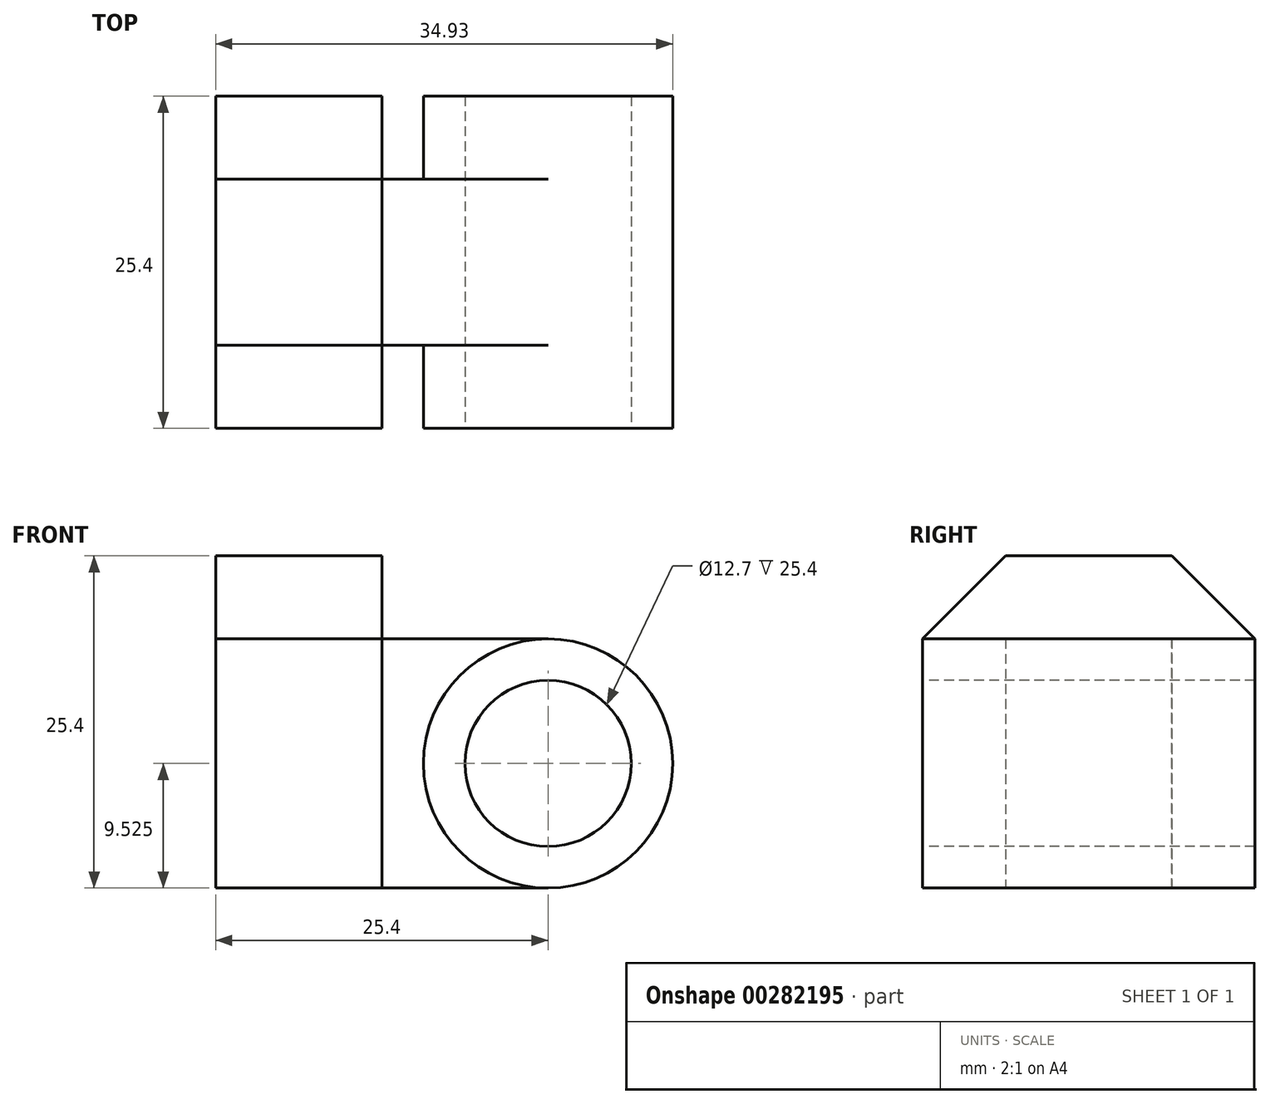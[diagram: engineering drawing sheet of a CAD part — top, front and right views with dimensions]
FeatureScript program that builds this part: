
annotation { "Feature Type Name" : "Feature", "Feature Type Description" : "" }
export const myFeature = defineFeature(function(context is Context, id is Id, definition is map)
    precondition{}
    {
        {
            var Q0;
            Q0=qCreatedBy(makeId("Right.planeOp"),FACE);
            var sketch = newSketch(context, id + "F0", { "sketchPlane" : qUnion([Q0])});
            skLineSegment(sketch, "E0", {"start": v(-12.7, 0) * mm, "end": v(12.7, 0) * mm});
            skLineSegment(sketch, "E1", {"start": v(12.7, 0) * mm, "end": v(12.7, 19.05) * mm});
            skLineSegment(sketch, "E2", {"start": v(-12.7, 19.05) * mm, "end": v(-12.7, 0) * mm});
            skLineSegment(sketch, "E3", {"start": v(12.7, 19.05) * mm, "end": v(6.35, 25.4) * mm});
            skLineSegment(sketch, "E4", {"start": v(6.35, 25.4) * mm, "end": v(-6.35, 25.4) * mm});
            skLineSegment(sketch, "E5", {"start": v(-6.35, 25.4) * mm, "end": v(-12.7, 19.05) * mm});
            skLineSegment(sketch, "E6", {"start": v(0, 0) * mm, "end": v(0, 25.4) * mm, "construction": true});
            skSolve(sketch);
        }
        {
            var Q0;
            Q0=makeQuery(id+"F0.imprint","IMPRINT",FACE,{"disambiguationData":[TD([[makeQuery(id+"F0.imprint","IMPRINT",EDGE,{"derivedFrom":sQuery(id+"F0.wireOp",EDGE,"E0")}),1.0]])]});
            extrude(context, id + "F1", {"entities" : qUnion([Q0]), "depth" : 12.7 * mm});
        }
        {
            var Q0;
            Q0=makeQuery(id+"F1.opExtrude","CAP_FACE",FACE,{"disambiguationData":[OSD([sQuery(id+"F0.wireOp",EDGE,"E0"),sQuery(id+"F0.wireOp",EDGE,"E1"),sQuery(id+"F0.wireOp",EDGE,"E2"),sQuery(id+"F0.wireOp",EDGE,"E3"),sQuery(id+"F0.wireOp",EDGE,"E4"),sQuery(id+"F0.wireOp",EDGE,"E5")])],"isStart":false});
            var sketch = newSketch(context, id + "F2", { "sketchPlane" : qUnion([Q0])});
            skLineSegment(sketch, "E7.bottom", {"start": v(-6.35, 19.05) * mm, "end": v(6.35, 19.05) * mm});
            skLineSegment(sketch, "E7.top", {"start": v(-6.35, 0) * mm, "end": v(6.35, 0) * mm});
            skLineSegment(sketch, "E7.left", {"start": v(-6.35, 19.05) * mm, "end": v(-6.35, 0) * mm});
            skLineSegment(sketch, "E7.right", {"start": v(6.35, 19.05) * mm, "end": v(6.35, 0) * mm});
            skSolve(sketch);
        }
        {
            var Q0;
            Q0=makeQuery(id+"F2.imprint","IMPRINT",FACE,{"disambiguationData":[TD([[makeQuery(id+"F2.imprint","IMPRINT",EDGE,{"derivedFrom":sQuery(id+"F2.wireOp",EDGE,"E7.bottom")}),-1.0]])]});
            extrude(context, id + "F3", {"entities" : qUnion([Q0]), "operationType" : NewBodyOperationType.ADD, "depth" : 12.7 * mm});
        }
        {
            var Q0;
            Q0=makeQuery(id+"F3.opExtrude","SWEPT_FACE",FACE,{"disambiguationData":[OSD([sQuery(id+"F2.wireOp",EDGE,"E7.left")])]});
            var sketch = newSketch(context, id + "F4", { "sketchPlane" : qUnion([Q0])});
            skCircle(sketch, "E8", {"center": v(25.4, 9.53) * mm, "radius": 6.35 * mm});
            skCircle(sketch, "E9", {"center": v(25.4, 9.53) * mm, "radius": 9.53 * mm});
            skSolve(sketch);
        }
        {
            var Q0;
            {var subQ0=sQuery(id+"F4.wireOp",EDGE,"E8");var subQ1=makeQuery(id+"F3.opExtrude","CAP_EDGE",EDGE,{"disambiguationData":[OSD([sQuery(id+"F2.wireOp",EDGE,"E7.left")])],"isStart":false});var subQ2=makeQuery(id+"F4.imprint","INTERSECT",VERTEX,{"disambiguationData":[OD(0.0)],"derivedFrom":[subQ1,subQ0]});Q0=makeQuery(id+"F4.imprint","IMPRINT",FACE,{"disambiguationData":[TD([[makeQuery(id+"F4.imprint","IMPRINT",EDGE,{"disambiguationData":[TD([[subQ2,-1.0]])],"derivedFrom":subQ0}),1.0]])]});}
            extrude(context, id + "F5", {"entities" : qUnion([Q0]), "operationType" : NewBodyOperationType.REMOVE, "oppositeDirection" : true, "depth" : 25.4 * mm});
        }
        {
            var Q0;
            {var subQ0=sQuery(id+"F4.wireOp",EDGE,"E8");var subQ1=sQuery(id+"F2.wireOp",EDGE,"E7.left");var subQ2=makeQuery(id+"F3.opExtrude","CAP_EDGE",EDGE,{"disambiguationData":[OSD([subQ1])],"isStart":false});var subQ3=makeQuery(id+"F4.imprint","INTERSECT",VERTEX,{"disambiguationData":[OD(0.0)],"derivedFrom":[subQ2,subQ0]});Q0=makeQuery(id+"F4.imprint","IMPRINT",FACE,{"disambiguationData":[TD([[makeQuery(id+"F4.imprint","IMPRINT",EDGE,{"disambiguationData":[TD([[subQ3,1.0]])],"derivedFrom":subQ0}),-1.0]])]});}
            extrude(context, id + "F6", {"entities" : qUnion([Q0]), "operationType" : NewBodyOperationType.ADD, "oppositeDirection" : true, "depth" : 19.05 * mm});
        }
        {
            var Q0;
            {var subQ0=sQuery(id+"F4.wireOp",EDGE,"E8");var subQ1=sQuery(id+"F2.wireOp",EDGE,"E7.left");var subQ2=makeQuery(id+"F3.opExtrude","CAP_EDGE",EDGE,{"disambiguationData":[OSD([subQ1])],"isStart":false});var subQ3=makeQuery(id+"F4.imprint","INTERSECT",VERTEX,{"disambiguationData":[OD(0.0)],"derivedFrom":[subQ2,subQ0]});Q0=makeQuery(id+"F4.imprint","IMPRINT",FACE,{"disambiguationData":[TD([[makeQuery(id+"F4.imprint","IMPRINT",EDGE,{"disambiguationData":[TD([[subQ3,1.0]])],"derivedFrom":subQ0}),-1.0]])]});}
            extrude(context, id + "F7", {"entities" : qUnion([Q0]), "operationType" : NewBodyOperationType.ADD, "depth" : 6.35 * mm});
        }
        {
            var Q0;
            {var subQ0=sQuery(id+"F4.wireOp",EDGE,"E8");var subQ1=sQuery(id+"F2.wireOp",EDGE,"E7.left");var subQ2=makeQuery(id+"F3.opExtrude","CAP_EDGE",EDGE,{"disambiguationData":[OSD([subQ1])],"isStart":false});var subQ3=makeQuery(id+"F4.imprint","INTERSECT",VERTEX,{"disambiguationData":[OD(0.0)],"derivedFrom":[subQ2,subQ0]});Q0=makeQuery(id+"F4.imprint","IMPRINT",FACE,{"disambiguationData":[TD([[makeQuery(id+"F4.imprint","IMPRINT",EDGE,{"disambiguationData":[TD([[subQ3,-1.0]])],"derivedFrom":subQ0}),-1.0]])]});}
            extrude(context, id + "F8", {"entities" : qUnion([Q0]), "operationType" : NewBodyOperationType.ADD, "depth" : 6.35 * mm});
        }
        {
            var Q0;
            {var subQ0=sQuery(id+"F4.wireOp",EDGE,"E8");var subQ1=sQuery(id+"F2.wireOp",EDGE,"E7.left");var subQ2=makeQuery(id+"F3.opExtrude","CAP_EDGE",EDGE,{"disambiguationData":[OSD([subQ1])],"isStart":false});var subQ3=makeQuery(id+"F4.imprint","INTERSECT",VERTEX,{"disambiguationData":[OD(0.0)],"derivedFrom":[subQ2,subQ0]});Q0=makeQuery(id+"F4.imprint","IMPRINT",FACE,{"disambiguationData":[TD([[makeQuery(id+"F4.imprint","IMPRINT",EDGE,{"disambiguationData":[TD([[subQ3,-1.0]])],"derivedFrom":subQ0}),-1.0]])]});}
            extrude(context, id + "F9", {"entities" : qUnion([Q0]), "operationType" : NewBodyOperationType.ADD, "oppositeDirection" : true, "depth" : 19.05 * mm});
        }
    });
